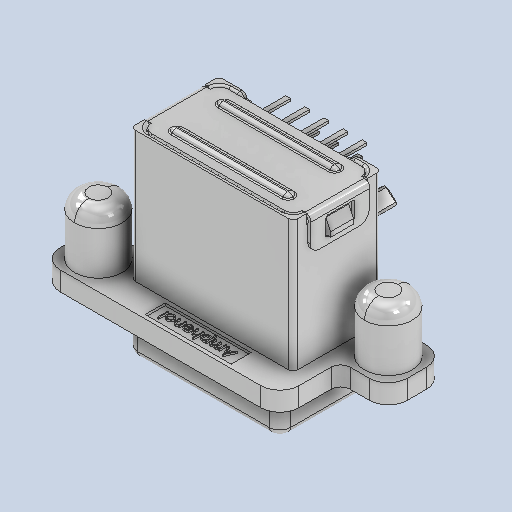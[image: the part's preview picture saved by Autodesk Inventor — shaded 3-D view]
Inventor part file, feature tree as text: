
AUTODESK INVENTOR PART (.ipt)
format: ipt  version: 2024.2 (Build 282272000, 272)  size: 4,688,384 bytes
history: native  units: mm
features: other x2, surface_op x1, plane x1
ambient origin geometry x8: Origin, YZ Plane, XZ Plane, XY Plane, X Axis, Y Axis, Z Axis, Center Point
bodies: Solid1 (feature_tree)
feature tree (4):
  surface_op  "Stitch Surface1"
  plane  "Work Plane1"
  other  "Composite1"
  other  "Srf1"
